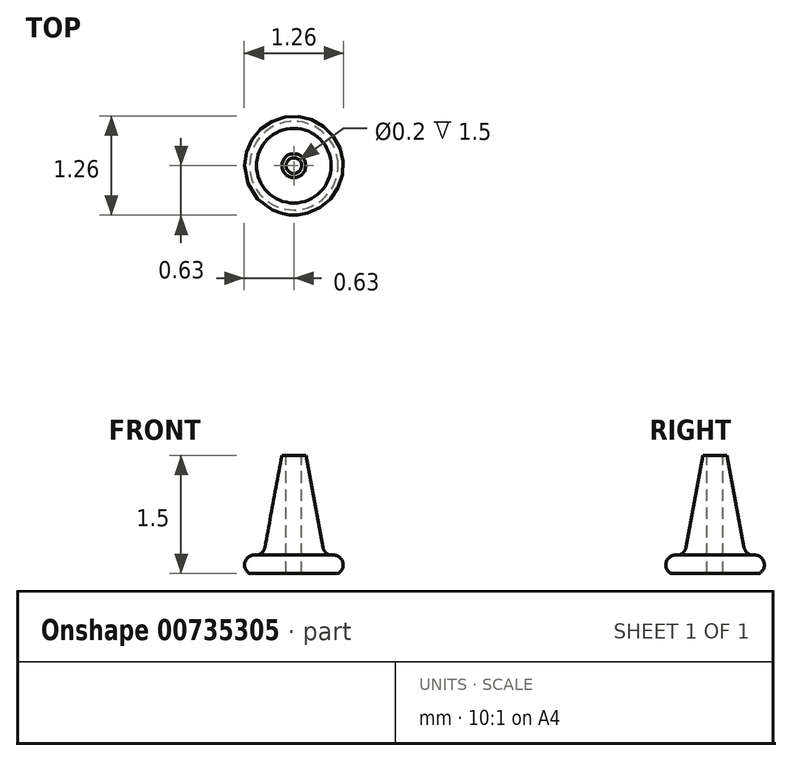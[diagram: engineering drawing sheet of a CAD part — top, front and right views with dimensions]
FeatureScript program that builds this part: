
annotation { "Feature Type Name" : "Feature", "Feature Type Description" : "" }
export const myFeature = defineFeature(function(context is Context, id is Id, definition is map)
    precondition{}
    {
        {
            var Q0;
            Q0=qCreatedBy(makeId("Front.planeOp"),FACE);
            var sketch = newSketch(context, id + "F0", { "sketchPlane" : qUnion([Q0])});
            skLineSegment(sketch, "E0", {"start": v(0, 0) * mm, "end": v(0, 1.5) * mm});
            skLineSegment(sketch, "E1", {"start": v(0, 1.5) * mm, "end": v(-0.15, 1.5) * mm});
            skLineSegment(sketch, "E2", {"start": v(-0.56, 0) * mm, "end": v(0, 0) * mm});
            skLineSegment(sketch, "E3", {"start": v(-0.15, 1.5) * mm, "end": v(-0.37, 0.33) * mm});
            skArc(sketch, "E4", {"start": v(-0.47, 0.23) * mm, "mid": v(-0.4, 0.26) * mm, "end": v(-0.37, 0.33) * mm});
            skArc(sketch, "E5", {"start": v(-0.47, 0.23) * mm, "mid": v(-0.62, 0.15) * mm, "end": v(-0.56, 0) * mm});
            skSolve(sketch);
        }
        {
            var Q0;
            Q0 = qSketchRegion(id + "F0", true);
            var Q1;
            Q1=sQuery(id+"F0.wireOp",EDGE,"E0");
            revolve(context, id + "F1", {"surfaceOperationType" : NewSurfaceOperationType.NEW, "entities" : qUnion([Q0]), "axis" : qUnion([Q1]), "revolveType" : RevolveType.FULL});
        }
        {
            var Q0;
            Q0=makeQuery(id+"F1.opRevolve","SWEPT_FACE",FACE,{"disambiguationData":[OSD([sQuery(id+"F0.wireOp",EDGE,"E1")])]});
            var sketch = newSketch(context, id + "F2", { "sketchPlane" : qUnion([Q0])});
            skCircle(sketch, "E6", {"center": v(0, 0) * mm, "radius": 0.1 * mm});
            skSolve(sketch);
        }
        {
            var Q0;
            Q0 = qSketchRegion(id + "F2", true);
            extrude(context, id + "F3", {"entities" : qUnion([Q0]), "operationType" : NewBodyOperationType.REMOVE, "oppositeDirection" : true, "depth" : 1.5 * mm, "offsetDistance" : 25 * mm});
        }
    });
